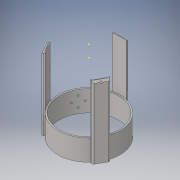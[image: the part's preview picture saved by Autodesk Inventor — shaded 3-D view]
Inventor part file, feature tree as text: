
AUTODESK INVENTOR PART (.ipt)
format: ipt  version: 2016 (Build 200138000, 138)  size: 270,848 bytes
history: native  units: in
note: dims shown in document units (in); Inventor stores cm internally (conversion verified against a paired STEP export)
features: sketch x18, extrude x15, plane x3, chamfer x2, fillet x1, revolve x1
ambient origin geometry x8: Origin, YZ Plane, XZ Plane, XY Plane, X Axis, Y Axis, Z Axis, Center Point
bodies: Solid1 (feature_tree)
feature tree (40):
  extrude  "Extrusion1"  Depth=0.3in TaperAngle=0.0deg
  extrude  "Extrusion2"  Depth=0.125in TaperAngle=0.0deg
  extrude  "Extrusion3"  Depth=3.875in
  sketch  "Sketch4"  dims[d9=0.125in d10=0.0in d11=4.0in]
  extrude  "Extrusion4"  Depth=4.0in
  extrude  "Extrusion5"  Depth=4.5in
  extrude  "Extrusion6"  Depth=0.1in TaperAngle=45.0deg
  chamfer  "Chamfer1"  Distance=2.3622in Angle=360.0deg
  extrude  "Extrusion7"  Depth=1.0in
  extrude  "Extrusion8"  Depth=5.0in TaperAngle=0.0deg
  extrude  "Extrusion9"  Depth=0.375in TaperAngle=0.0deg
  extrude  "Extrusion10"  Depth=0.375in TaperAngle=0.0deg
  extrude  "Extrusion11"  Depth=0.5in
  sketch  "Sketch13"  dims[d39=20.0in d40=0.0in d41=0.5in]
  extrude  "Extrusion12"  Depth=0.15in
  chamfer  "Chamfer2"  Distance=1.1811in Angle=360.0deg
  fillet  "Fillet1"  Radius=0.125in
  plane  "Work Plane1"
  revolve  "Revolution1"  [1 undecoded]
  plane  "Work Plane3"
  extrude  "Extrusion13"  [1 undecoded]
  extrude  "Extrusion15"  Depth=0.118in
  extrude  "Extrusion16"  Depth=0.118in
  sketch  "Sketch1"  dims[d0=4.0in d1=0.3in d2=0.0in]
  sketch  "Sketch2"  dims[d3=3.875in d4=0.125in d5=0.0in]
  sketch  "Sketch3"  dims[d6=0.3in d7=0.0in d8=3.875in]
  sketch  "Sketch5"  dims[d12=0.2in d13=0.0in d14=4.5in]
  sketch  "Sketch6"  dims[d15=0.24in d16=0.0in d17=0.1in d18=0.125in d19=45.0deg]
  sketch  "Sketch7"  dims[d20=0.138in]
  sketch  "Sketch8"  dims[d21=2.125in d22=2.3622in d24=360.0deg]
  sketch  "Sketch9"  dims[d26=0.24in d27=0.0in d28=1.0in]
  sketch  "Sketch10"  dims[d29=0.1in d31=5.0in d32=0.0in]
  sketch  "Sketch11"  dims[d33=3.0in d34=0.375in d35=0.0in]
  sketch  "Sketch12"  dims[d36=1.0in d37=0.375in d38=0.0in]
  sketch  "Sketch14"  dims[d42=0.5in d43=0.15in d44=1.1811in d46=360.0deg]
  sketch  "Sketch15"  dims[d48=5.0in d49=0.2in d50=0.0in d51=0.0in]
  plane  "Work Plane2"
  sketch  "Sketch16"  dims[d52=0.125in d53=0.125in d54=45.0deg d55=0.125in]
  sketch  "Sketch18"  dims[d58=0.1in d59=1.527in]
  sketch  "Sketch19"  dims[d60=90.0deg d61=-4.125in d64=0.118in d65=0.118in d66=0.118in d67=0.118in d68=0.74in d69=0.74in d70=0.74in d71=0.74in d72=5.0in d73=0.0in d78=1.04in d79=0.0in d80=0.1181in d81=1.0in d82=0.0in]
note: 2 required parameter values undecoded (feature->parameter linkage not recoverable at this tier; creation-order binding heuristic only, values carry confidence <= 0.55)